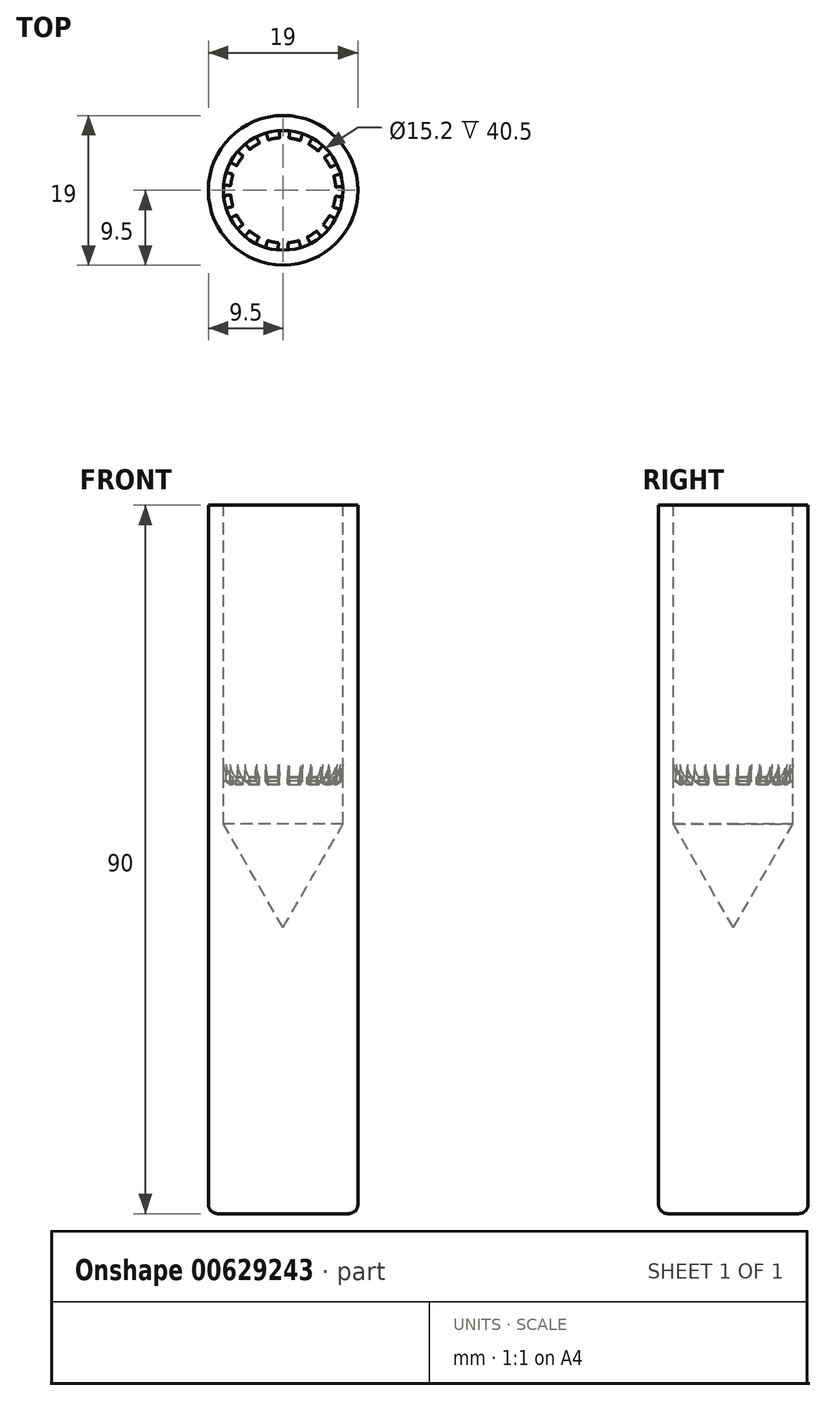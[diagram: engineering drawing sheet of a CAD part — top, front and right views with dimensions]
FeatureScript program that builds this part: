
annotation { "Feature Type Name" : "Feature", "Feature Type Description" : "" }
export const myFeature = defineFeature(function(context is Context, id is Id, definition is map)
    precondition{}
    {
        {
            var Q0;
            Q0=qCreatedBy(makeId("Front.planeOp"),FACE);
            var sketch = newSketch(context, id + "F0", { "sketchPlane" : qUnion([Q0])});
            skLineSegment(sketch, "E0", {"start": v(0, 0) * mm, "end": v(-9.5, 0) * mm});
            skLineSegment(sketch, "E1", {"start": v(-9.5, 0) * mm, "end": v(-9.5, 90) * mm});
            skLineSegment(sketch, "E2", {"start": v(-9.5, 90) * mm, "end": v(-7.6, 90) * mm});
            skLineSegment(sketch, "E3", {"start": v(-7.6, 90) * mm, "end": v(-7.6, 57.09) * mm});
            skLineSegment(sketch, "E4", {"start": v(0, 2) * mm, "end": v(0, 0) * mm});
            skLineSegment(sketch, "E5", {"start": v(-7.6, 54.88) * mm, "end": v(-7.6, 53.5) * mm, "construction": true});
            skLineSegment(sketch, "E6", {"start": v(-6.7, 79.96) * mm, "end": v(-6.7, 49.14) * mm, "construction": true});
            skLineSegment(sketch, "E7", {"start": v(-7.25, 89.43) * mm, "end": v(-7.25, 57.62) * mm, "construction": true});
            skLineSegment(sketch, "E8", {"start": v(-7.6, 49.5) * mm, "end": v(0, 49.5) * mm, "construction": true});
            skLineSegment(sketch, "E9", {"start": v(0, 49.5) * mm, "end": v(0, 2) * mm});
            skLineSegment(sketch, "E10", {"start": v(-7.6, 49.5) * mm, "end": v(-7.6, 53.5) * mm});
            skLineSegment(sketch, "E11", {"start": v(-6.74, 55.44) * mm, "end": v(-6.69, 55.4) * mm});
            skLineSegment(sketch, "E12", {"start": v(-6.7, 55.37) * mm, "end": v(-6.7, 54.63) * mm});
            skLineSegment(sketch, "E13", {"start": v(-6.84, 54.55) * mm, "end": v(-7.46, 54.96) * mm});
            skLineSegment(sketch, "E14", {"start": v(-7.6, 54.88) * mm, "end": v(-7.6, 53.5) * mm});
            skPoint(sketch, "E15.visualSharp", {"position": v(-7.6, 56) * mm});
            skArc(sketch, "E15.filletArc", {"start": v(-7.6, 57.09) * mm, "mid": v(-7.36, 56.13) * mm, "end": v(-6.69, 55.4) * mm});
            skArc(sketch, "E16.filletArc", {"start": v(-7.46, 54.96) * mm, "mid": v(-7.55, 54.96) * mm, "end": v(-7.6, 54.88) * mm});
            skPoint(sketch, "E17.visualSharp", {"position": v(-6.7, 55.42) * mm});
            skArc(sketch, "E17.filletArc", {"start": v(-6.7, 55.37) * mm, "mid": v(-6.71, 55.41) * mm, "end": v(-6.74, 55.44) * mm});
            skPoint(sketch, "E18.visualSharp", {"position": v(-6.7, 54.46) * mm});
            skArc(sketch, "E18.filletArc", {"start": v(-6.84, 54.55) * mm, "mid": v(-6.75, 54.55) * mm, "end": v(-6.7, 54.63) * mm});
            skLineSegment(sketch, "E19", {"start": v(-7.6, 49.5) * mm, "end": v(0, 36.34) * mm});
            skSolve(sketch);
        }
        {
            var Q0;
            Q0 = qSketchRegion(id + "F0", true);
            var Q1;
            Q1=sQuery(id+"F0.wireOp",EDGE,"E4");
            revolve(context, id + "F1", {"entities" : qUnion([Q0]), "axis" : qUnion([Q1]), "revolveType" : RevolveType.FULL});
        }
        {
            var Q0;
            Q0=makeQuery(id+"F1.opRevolve","SWEPT_FACE",FACE,{"disambiguationData":[OSD([sQuery(id+"F0.wireOp",EDGE,"E0")])]});
            fillet(context, id + "F2", {"entities" : qUnion([Q0]), "radius" : 1.2 * mm, "tangentPropagation" : true, "allowEdgeOverflow" : false});
        }
        {
            var Q0;
            Q0=qCreatedBy(makeId("Front.planeOp"),FACE);
            var sketch = newSketch(context, id + "F3", { "sketchPlane" : qUnion([Q0])});
            skPoint(sketch, "E20.0", {"position": v(-7.6, 57.09) * mm});
            skPoint(sketch, "E21.0", {"position": v(-7.6, 53.5) * mm});
            skLineSegment(sketch, "E22.bottom", {"start": v(-7.6, 57.09) * mm, "end": v(0, 57.09) * mm});
            skLineSegment(sketch, "E22.top", {"start": v(-7.6, 53.5) * mm, "end": v(0, 53.5) * mm});
            skLineSegment(sketch, "E22.left", {"start": v(-7.6, 57.09) * mm, "end": v(-7.6, 53.5) * mm});
            skLineSegment(sketch, "E22.right", {"start": v(0, 57.09) * mm, "end": v(0, 53.5) * mm});
            skSolve(sketch);
        }
        {
            var Q0;
            Q0 = qSketchRegion(id + "F3", true);
            var Q1;
            Q1=sQuery(id+"F3.wireOp",EDGE,"E22.right");
            revolve(context, id + "F4", {"entities" : qUnion([Q0]), "axis" : qUnion([Q1]), "revolveType" : RevolveType.FULL});
        }
        {
            var Q0;
            Q0=makeQuery(id+"F4.opRevolve","SWEPT_FACE",FACE,{"disambiguationData":[OSD([sQuery(id+"F3.wireOp",EDGE,"E22.bottom")])]});
            var sketch = newSketch(context, id + "F5", { "sketchPlane" : qUnion([Q0])});
            skCircle(sketch, "E23.0", {"center": v(0, 0) * mm, "radius": 7.6 * mm, "construction": true});
            skLineSegment(sketch, "E24", {"start": v(0, 0) * mm, "end": v(1.25, -14.3) * mm});
            skLineSegment(sketch, "E25", {"start": v(1.25, -14.3) * mm, "end": v(-1.25, -14.3) * mm});
            skLineSegment(sketch, "E26", {"start": v(-1.25, -14.3) * mm, "end": v(0, 0) * mm});
            skLineSegment(sketch, "E27.1.0", {"start": v(-0.03, -0.04) * mm, "end": v(6.6, -12.77) * mm});
            skLineSegment(sketch, "E27.1.1", {"start": v(6.6, -12.77) * mm, "end": v(4.3, -13.72) * mm});
            skLineSegment(sketch, "E27.1.2", {"start": v(4.3, -13.72) * mm, "end": v(-0.03, -0.04) * mm});
            skLineSegment(sketch, "E27.2.0", {"start": v(-0.03, -0.08) * mm, "end": v(10.96, -9.3) * mm});
            skLineSegment(sketch, "E27.2.1", {"start": v(10.96, -9.3) * mm, "end": v(9.2, -11.08) * mm});
            skLineSegment(sketch, "E27.2.2", {"start": v(9.2, -11.08) * mm, "end": v(-0.03, -0.08) * mm});
            skLineSegment(sketch, "E27.3.0", {"start": v(-0.03, -0.13) * mm, "end": v(13.66, -4.44) * mm});
            skLineSegment(sketch, "E27.3.1", {"start": v(13.66, -4.44) * mm, "end": v(12.7, -6.75) * mm});
            skLineSegment(sketch, "E27.3.2", {"start": v(12.7, -6.75) * mm, "end": v(-0.03, -0.13) * mm});
            skLineSegment(sketch, "E27.4.0", {"start": v(0, -0.16) * mm, "end": v(14.3, 1.09) * mm});
            skLineSegment(sketch, "E27.4.1", {"start": v(14.3, 1.09) * mm, "end": v(14.3, -1.41) * mm});
            skLineSegment(sketch, "E27.4.2", {"start": v(14.3, -1.41) * mm, "end": v(0, -0.16) * mm});
            skLineSegment(sketch, "E27.5.0", {"start": v(0.04, -0.19) * mm, "end": v(12.77, 6.44) * mm});
            skLineSegment(sketch, "E27.5.1", {"start": v(12.77, 6.44) * mm, "end": v(13.72, 4.13) * mm});
            skLineSegment(sketch, "E27.5.2", {"start": v(13.72, 4.13) * mm, "end": v(0.04, -0.19) * mm});
            skLineSegment(sketch, "E27.6.0", {"start": v(0.08, -0.2) * mm, "end": v(9.3, 10.8) * mm});
            skLineSegment(sketch, "E27.6.1", {"start": v(9.3, 10.8) * mm, "end": v(11.08, 9.03) * mm});
            skLineSegment(sketch, "E27.6.2", {"start": v(11.08, 9.03) * mm, "end": v(0.08, -0.2) * mm});
            skLineSegment(sketch, "E27.7.0", {"start": v(0.13, -0.19) * mm, "end": v(4.44, 13.5) * mm});
            skLineSegment(sketch, "E27.7.1", {"start": v(4.44, 13.5) * mm, "end": v(6.75, 12.54) * mm});
            skLineSegment(sketch, "E27.7.2", {"start": v(6.75, 12.54) * mm, "end": v(0.13, -0.19) * mm});
            skPoint(sketch, "E27.center", {"position": v(0.08, -0.08) * mm});
            skLineSegment(sketch, "E28.3.8.0", {"start": v(-1.09, 14.13) * mm, "end": v(1.41, 14.13) * mm});
            skLineSegment(sketch, "E28.5.8.0", {"start": v(0.16, -0.16) * mm, "end": v(-1.09, 14.13) * mm});
            skLineSegment(sketch, "E28.6.8.0", {"start": v(1.41, 14.13) * mm, "end": v(0.16, -0.16) * mm});
            skLineSegment(sketch, "E28.3.9.0", {"start": v(-6.44, 12.6) * mm, "end": v(-4.13, 13.56) * mm});
            skLineSegment(sketch, "E28.5.9.0", {"start": v(0.19, -0.13) * mm, "end": v(-6.44, 12.6) * mm});
            skLineSegment(sketch, "E28.6.9.0", {"start": v(-4.13, 13.56) * mm, "end": v(0.19, -0.13) * mm});
            skLineSegment(sketch, "E29.3.10.0", {"start": v(-10.8, 9.14) * mm, "end": v(-9.03, 10.91) * mm});
            skLineSegment(sketch, "E29.5.10.0", {"start": v(0.2, -0.08) * mm, "end": v(-10.8, 9.14) * mm});
            skLineSegment(sketch, "E29.6.10.0", {"start": v(-9.03, 10.91) * mm, "end": v(0.2, -0.08) * mm});
            skLineSegment(sketch, "E29.3.11.0", {"start": v(-13.5, 4.28) * mm, "end": v(-12.54, 6.59) * mm});
            skLineSegment(sketch, "E29.5.11.0", {"start": v(0.19, -0.04) * mm, "end": v(-13.5, 4.28) * mm});
            skLineSegment(sketch, "E29.6.11.0", {"start": v(-12.54, 6.59) * mm, "end": v(0.19, -0.04) * mm});
            skCircle(sketch, "E30", {"center": v(0, 0) * mm, "radius": 4.29 * mm});
            skLineSegment(sketch, "E31.3.12.0", {"start": v(-14.13, -1.25) * mm, "end": v(-14.13, 1.25) * mm});
            skLineSegment(sketch, "E31.5.12.0", {"start": v(0.16, 0) * mm, "end": v(-14.13, -1.25) * mm});
            skLineSegment(sketch, "E31.6.12.0", {"start": v(-14.13, 1.25) * mm, "end": v(0.16, 0) * mm});
            skLineSegment(sketch, "E31.3.13.0", {"start": v(-12.6, -6.6) * mm, "end": v(-13.56, -4.3) * mm});
            skLineSegment(sketch, "E31.5.13.0", {"start": v(0.13, 0.03) * mm, "end": v(-12.6, -6.6) * mm});
            skLineSegment(sketch, "E31.6.13.0", {"start": v(-13.56, -4.3) * mm, "end": v(0.13, 0.03) * mm});
            skLineSegment(sketch, "E31.3.14.0", {"start": v(-9.14, -10.96) * mm, "end": v(-10.91, -9.2) * mm});
            skLineSegment(sketch, "E31.5.14.0", {"start": v(0.08, 0.03) * mm, "end": v(-9.14, -10.96) * mm});
            skLineSegment(sketch, "E31.6.14.0", {"start": v(-10.91, -9.2) * mm, "end": v(0.08, 0.03) * mm});
            skLineSegment(sketch, "E31.3.15.0", {"start": v(-4.28, -13.66) * mm, "end": v(-6.59, -12.7) * mm});
            skLineSegment(sketch, "E31.5.15.0", {"start": v(0.04, 0.03) * mm, "end": v(-4.28, -13.66) * mm});
            skLineSegment(sketch, "E31.6.15.0", {"start": v(-6.59, -12.7) * mm, "end": v(0.04, 0.03) * mm});
            skSolve(sketch);
        }
        {
            var Q0;
            Q0 = qSketchRegion(id + "F5", true);
            extrude(context, id + "F6", {"entities" : qUnion([Q0]), "oppositeDirection" : true, "depth" : 25 * mm, "offsetDistance" : 25 * mm});
        }
        {
            var Q0;
            Q0=makeQuery(id+"F4.opRevolve","SWEPT_BODY",BODY,{"disambiguationData":[OSD([sQuery(id+"F3.wireOp",EDGE,"E22.bottom"),sQuery(id+"F3.wireOp",EDGE,"E22.top"),sQuery(id+"F3.wireOp",EDGE,"E22.left"),sQuery(id+"F3.wireOp",EDGE,"E22.right")])]});
            var Q1;
            Q1=makeQuery(id+"F6.opExtrude","SWEPT_BODY",BODY,{"disambiguationData":[OSD([sQuery(id+"F5.wireOp",EDGE,"E24"),sQuery(id+"F5.wireOp",EDGE,"E25"),sQuery(id+"F5.wireOp",EDGE,"E26"),sQuery(id+"F5.wireOp",EDGE,"E27.1.0"),sQuery(id+"F5.wireOp",EDGE,"E27.1.1"),sQuery(id+"F5.wireOp",EDGE,"E27.1.2"),sQuery(id+"F5.wireOp",EDGE,"E27.2.0"),sQuery(id+"F5.wireOp",EDGE,"E27.2.1"),sQuery(id+"F5.wireOp",EDGE,"E27.2.2"),sQuery(id+"F5.wireOp",EDGE,"E27.3.0"),sQuery(id+"F5.wireOp",EDGE,"E27.3.1"),sQuery(id+"F5.wireOp",EDGE,"E27.3.2"),sQuery(id+"F5.wireOp",EDGE,"E27.4.0"),sQuery(id+"F5.wireOp",EDGE,"E27.4.1"),sQuery(id+"F5.wireOp",EDGE,"E27.4.2"),sQuery(id+"F5.wireOp",EDGE,"E27.5.0"),sQuery(id+"F5.wireOp",EDGE,"E27.5.1"),sQuery(id+"F5.wireOp",EDGE,"E27.5.2"),sQuery(id+"F5.wireOp",EDGE,"E27.6.0"),sQuery(id+"F5.wireOp",EDGE,"E27.6.1"),sQuery(id+"F5.wireOp",EDGE,"E27.6.2"),sQuery(id+"F5.wireOp",EDGE,"E27.7.0"),sQuery(id+"F5.wireOp",EDGE,"E27.7.1"),sQuery(id+"F5.wireOp",EDGE,"E27.7.2"),sQuery(id+"F5.wireOp",EDGE,"E28.3.8.0"),sQuery(id+"F5.wireOp",EDGE,"E28.5.8.0"),sQuery(id+"F5.wireOp",EDGE,"E28.6.8.0"),sQuery(id+"F5.wireOp",EDGE,"E28.3.9.0"),sQuery(id+"F5.wireOp",EDGE,"E28.5.9.0"),sQuery(id+"F5.wireOp",EDGE,"E28.6.9.0"),sQuery(id+"F5.wireOp",EDGE,"E29.3.10.0"),sQuery(id+"F5.wireOp",EDGE,"E29.5.10.0"),sQuery(id+"F5.wireOp",EDGE,"E29.6.10.0"),sQuery(id+"F5.wireOp",EDGE,"E29.3.11.0"),sQuery(id+"F5.wireOp",EDGE,"E29.5.11.0"),sQuery(id+"F5.wireOp",EDGE,"E29.6.11.0"),sQuery(id+"F5.wireOp",EDGE,"E30")])]});
            booleanBodies(context, id + "F7", {"operationType" : BooleanOperationType.INTERSECTION, "tools" : qUnion([Q0, Q1])});
        }
        {
            var Q0;
            Q0=makeQuery(id+"F7.opBoolean","INTERSECT",BODY,{"derivedFrom":[makeQuery(id+"F4.opRevolve","SWEPT_BODY",BODY,{"disambiguationData":[OSD([sQuery(id+"F3.wireOp",EDGE,"E22.bottom"),sQuery(id+"F3.wireOp",EDGE,"E22.top"),sQuery(id+"F3.wireOp",EDGE,"E22.left"),sQuery(id+"F3.wireOp",EDGE,"E22.right")])]}),makeQuery(id+"F6.opExtrude","SWEPT_BODY",BODY,{"disambiguationData":[OSD([sQuery(id+"F5.wireOp",EDGE,"E24"),sQuery(id+"F5.wireOp",EDGE,"E25"),sQuery(id+"F5.wireOp",EDGE,"E26"),sQuery(id+"F5.wireOp",EDGE,"E27.1.0"),sQuery(id+"F5.wireOp",EDGE,"E27.1.1"),sQuery(id+"F5.wireOp",EDGE,"E27.1.2"),sQuery(id+"F5.wireOp",EDGE,"E27.2.0"),sQuery(id+"F5.wireOp",EDGE,"E27.2.1"),sQuery(id+"F5.wireOp",EDGE,"E27.2.2"),sQuery(id+"F5.wireOp",EDGE,"E27.3.0"),sQuery(id+"F5.wireOp",EDGE,"E27.3.1"),sQuery(id+"F5.wireOp",EDGE,"E27.3.2"),sQuery(id+"F5.wireOp",EDGE,"E27.4.0"),sQuery(id+"F5.wireOp",EDGE,"E27.4.1"),sQuery(id+"F5.wireOp",EDGE,"E27.4.2"),sQuery(id+"F5.wireOp",EDGE,"E27.5.0"),sQuery(id+"F5.wireOp",EDGE,"E27.5.1"),sQuery(id+"F5.wireOp",EDGE,"E27.5.2"),sQuery(id+"F5.wireOp",EDGE,"E27.6.0"),sQuery(id+"F5.wireOp",EDGE,"E27.6.1"),sQuery(id+"F5.wireOp",EDGE,"E27.6.2"),sQuery(id+"F5.wireOp",EDGE,"E27.7.0"),sQuery(id+"F5.wireOp",EDGE,"E27.7.1"),sQuery(id+"F5.wireOp",EDGE,"E27.7.2"),sQuery(id+"F5.wireOp",EDGE,"E28.3.8.0"),sQuery(id+"F5.wireOp",EDGE,"E28.5.8.0"),sQuery(id+"F5.wireOp",EDGE,"E28.6.8.0"),sQuery(id+"F5.wireOp",EDGE,"E28.3.9.0"),sQuery(id+"F5.wireOp",EDGE,"E28.5.9.0"),sQuery(id+"F5.wireOp",EDGE,"E28.6.9.0"),sQuery(id+"F5.wireOp",EDGE,"E29.3.10.0"),sQuery(id+"F5.wireOp",EDGE,"E29.5.10.0"),sQuery(id+"F5.wireOp",EDGE,"E29.6.10.0"),sQuery(id+"F5.wireOp",EDGE,"E29.3.11.0"),sQuery(id+"F5.wireOp",EDGE,"E29.5.11.0"),sQuery(id+"F5.wireOp",EDGE,"E29.6.11.0"),sQuery(id+"F5.wireOp",EDGE,"E30")])]})]});
            var Q1;
            Q1=makeQuery(id+"F1.opRevolve","SWEPT_BODY",BODY,{"disambiguationData":[OSD([sQuery(id+"F0.wireOp",EDGE,"E0"),sQuery(id+"F0.wireOp",EDGE,"E1"),sQuery(id+"F0.wireOp",EDGE,"E2"),sQuery(id+"F0.wireOp",EDGE,"E3"),sQuery(id+"F0.wireOp",EDGE,"E4"),sQuery(id+"F0.wireOp",EDGE,"E8"),sQuery(id+"F0.wireOp",EDGE,"E9"),sQuery(id+"F0.wireOp",EDGE,"E10"),sQuery(id+"F0.wireOp",EDGE,"E11"),sQuery(id+"F0.wireOp",EDGE,"E12"),sQuery(id+"F0.wireOp",EDGE,"E13"),sQuery(id+"F0.wireOp",EDGE,"E14"),sQuery(id+"F0.wireOp",EDGE,"E15.filletArc"),sQuery(id+"F0.wireOp",EDGE,"E16.filletArc"),sQuery(id+"F0.wireOp",EDGE,"E17.filletArc"),sQuery(id+"F0.wireOp",EDGE,"E18.filletArc")])]});
            booleanBodies(context, id + "F8", {"operationType" : BooleanOperationType.SUBTRACTION, "tools" : qUnion([Q0]), "targets" : qUnion([Q1])});
        }
    });
